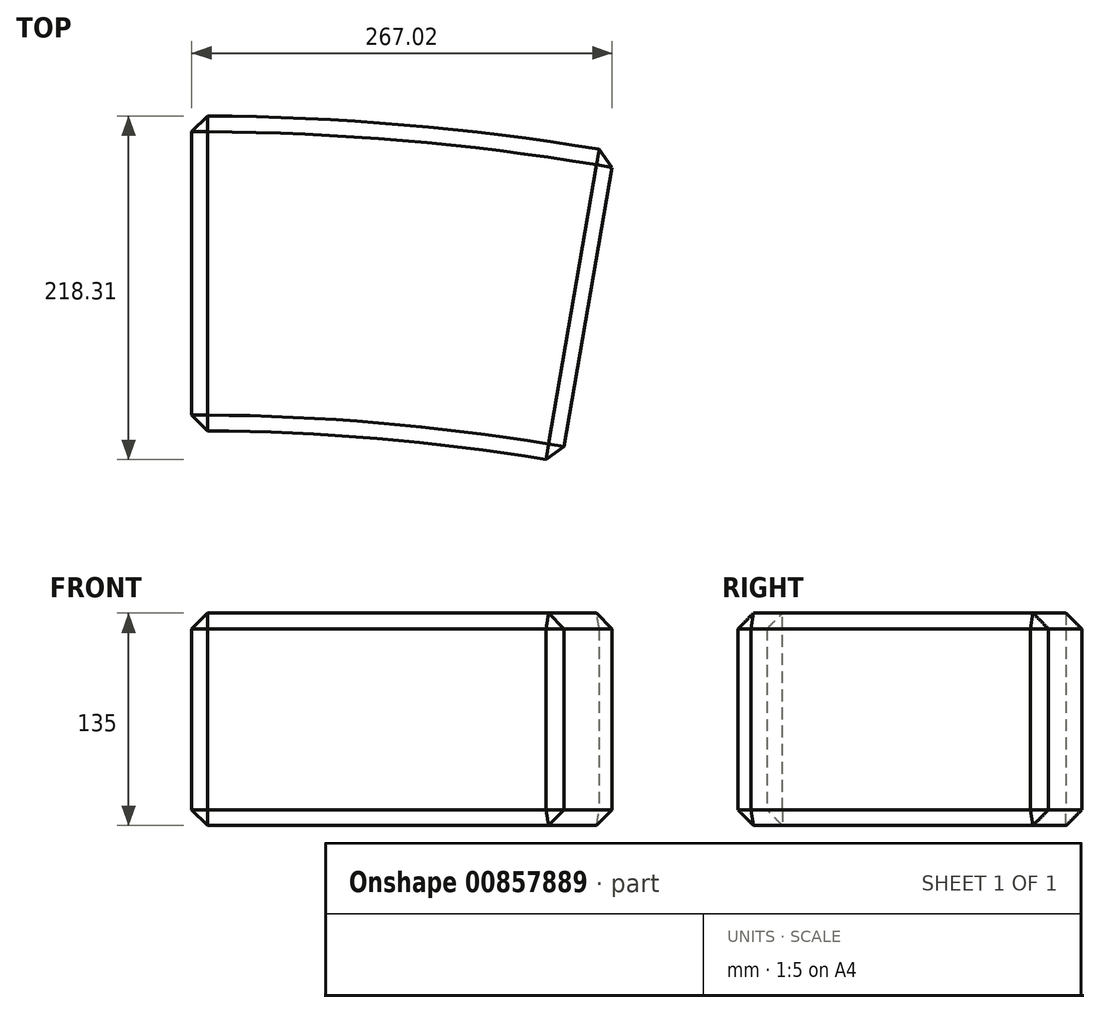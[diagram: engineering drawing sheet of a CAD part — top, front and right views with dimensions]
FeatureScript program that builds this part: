
annotation { "Feature Type Name" : "Feature", "Feature Type Description" : "" }
export const myFeature = defineFeature(function(context is Context, id is Id, definition is map)
    precondition{}
    {
        {
            var Q0;
            Q0=qCreatedBy(makeId("Top.planeOp"),FACE);
            var sketch = newSketch(context, id + "F0", { "sketchPlane" : qUnion([Q0])});
            skLineSegment(sketch, "E0", {"start": v(0, 0) * mm, "end": v(0, 200) * mm});
            skLineSegment(sketch, "E1", {"start": v(234.91, -20) * mm, "end": v(268.71, 177.13) * mm});
            skArc(sketch, "E2", {"start": v(234.91, -20) * mm, "mid": v(117.88, -5) * mm, "end": v(0, 0) * mm});
            skArc(sketch, "E3", {"start": v(268.71, 177.13) * mm, "mid": v(134.84, 194.27) * mm, "end": v(0, 200) * mm});
            skSolve(sketch);
        }
        {
            var Q0;
            Q0=makeQuery(id+"F0.imprint","IMPRINT",FACE,{"disambiguationData":[TD([[makeQuery(id+"F0.imprint","IMPRINT",EDGE,{"derivedFrom":sQuery(id+"F0.wireOp",EDGE,"E0")}),-1.0]])]});
            extrude(context, id + "F1", {"entities" : qUnion([Q0]), "depth" : 135 * mm, "offsetDistance" : 25 * mm});
        }
        {
            var Q0;
            Q0=makeQuery(id+"F1.opExtrude","CAP_EDGE",EDGE,{"disambiguationData":[OSD([sQuery(id+"F0.wireOp",EDGE,"E2")])],"isStart":false});
            var Q1;
            Q1=makeQuery(id+"F1.opExtrude","CAP_EDGE",EDGE,{"disambiguationData":[OSD([sQuery(id+"F0.wireOp",EDGE,"E1")])],"isStart":false});
            var Q2;
            Q2=makeQuery(id+"F1.opExtrude","CAP_EDGE",EDGE,{"disambiguationData":[OSD([sQuery(id+"F0.wireOp",EDGE,"E3")])],"isStart":false});
            var Q3;
            Q3=makeQuery(id+"F1.opExtrude","CAP_EDGE",EDGE,{"disambiguationData":[OSD([sQuery(id+"F0.wireOp",EDGE,"E0")])],"isStart":false});
            var Q4;
            Q4=makeQuery(id+"F1.opExtrude","SWEPT_EDGE",EDGE,{"disambiguationData":[OSD([sQuery(id+"F0.wireOp",EDGE,"E0"),sQuery(id+"F0.wireOp",EDGE,"E2")])]});
            var Q5;
            Q5=makeQuery(id+"F1.opExtrude","SWEPT_EDGE",EDGE,{"disambiguationData":[OSD([sQuery(id+"F0.wireOp",EDGE,"E1"),sQuery(id+"F0.wireOp",EDGE,"E2")])]});
            var Q6;
            Q6=makeQuery(id+"F1.opExtrude","SWEPT_EDGE",EDGE,{"disambiguationData":[OSD([sQuery(id+"F0.wireOp",EDGE,"E1"),sQuery(id+"F0.wireOp",EDGE,"E3")])]});
            var Q7;
            Q7=makeQuery(id+"F1.opExtrude","CAP_EDGE",EDGE,{"disambiguationData":[OSD([sQuery(id+"F0.wireOp",EDGE,"E2")])],"isStart":true});
            var Q8;
            Q8=makeQuery(id+"F1.opExtrude","CAP_EDGE",EDGE,{"disambiguationData":[OSD([sQuery(id+"F0.wireOp",EDGE,"E1")])],"isStart":true});
            var Q9;
            Q9=makeQuery(id+"F1.opExtrude","CAP_EDGE",EDGE,{"disambiguationData":[OSD([sQuery(id+"F0.wireOp",EDGE,"E3")])],"isStart":true});
            var Q10;
            Q10=makeQuery(id+"F1.opExtrude","CAP_EDGE",EDGE,{"disambiguationData":[OSD([sQuery(id+"F0.wireOp",EDGE,"E0")])],"isStart":true});
            var Q11;
            Q11=makeQuery(id+"F1.opExtrude","SWEPT_EDGE",EDGE,{"disambiguationData":[OSD([sQuery(id+"F0.wireOp",EDGE,"E0"),sQuery(id+"F0.wireOp",EDGE,"E3")])]});
            chamfer(context, id + "F2", {"entities" : qUnion([Q0, Q1, Q2, Q3, Q4, Q5, Q6, Q7, Q8, Q9, Q10, Q11]), "width" : 10 * mm, "tangentPropagation" : true});
        }
    });
